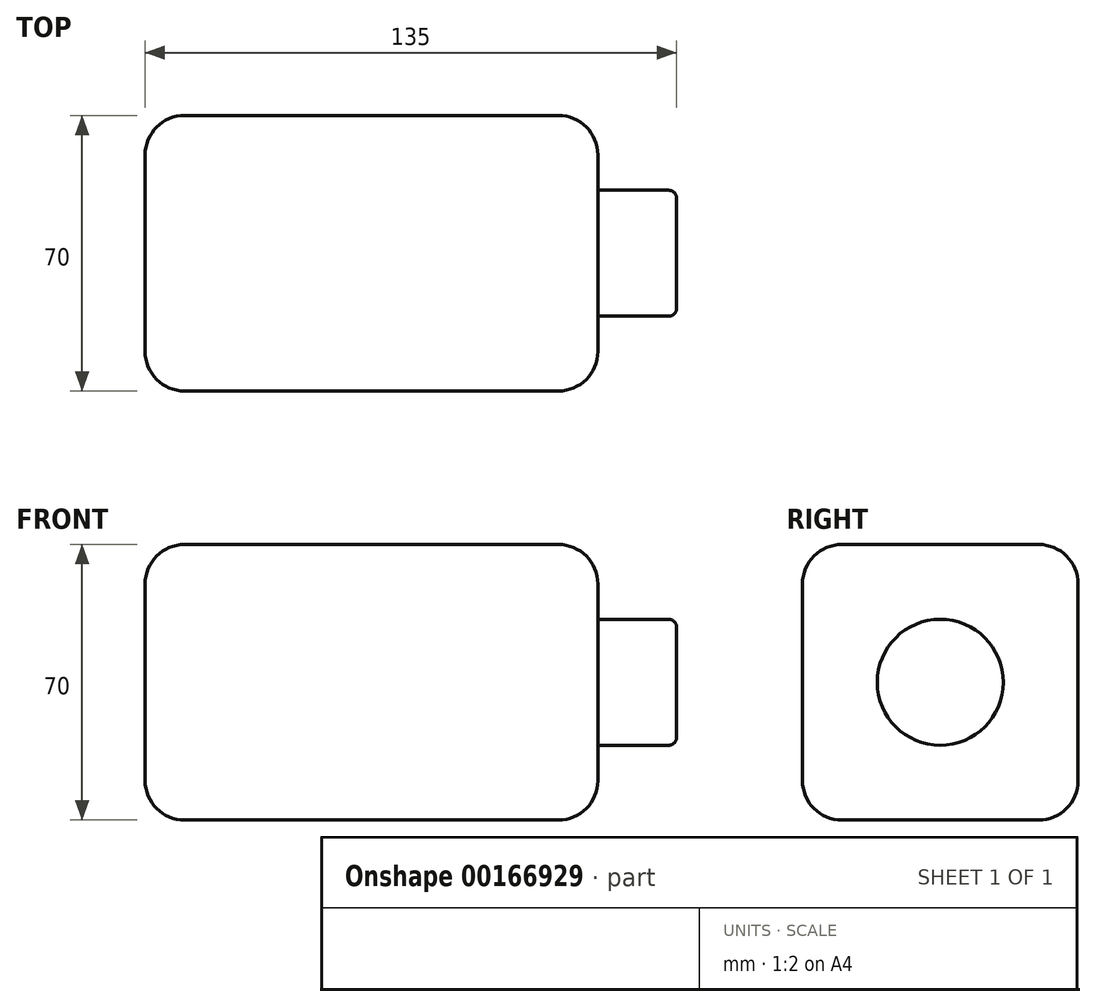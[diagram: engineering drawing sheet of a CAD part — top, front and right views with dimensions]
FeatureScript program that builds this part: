
annotation { "Feature Type Name" : "Feature", "Feature Type Description" : "" }
export const myFeature = defineFeature(function(context is Context, id is Id, definition is map)
    precondition{}
    {
        {
            var Q0;
            Q0=qCreatedBy(makeId("Right.planeOp"),FACE);
            var sketch = newSketch(context, id + "F0", { "sketchPlane" : qUnion([Q0])});
            skLineSegment(sketch, "E0.bottom", {"start": v(35, 35) * mm, "end": v(-35, 35) * mm});
            skLineSegment(sketch, "E0.top", {"start": v(35, -35) * mm, "end": v(-35, -35) * mm});
            skLineSegment(sketch, "E0.left", {"start": v(35, 35) * mm, "end": v(35, -35) * mm});
            skLineSegment(sketch, "E0.right", {"start": v(-35, 35) * mm, "end": v(-35, -35) * mm});
            skPoint(sketch, "E0.middle", {"position": v(0, 0) * mm});
            skSolve(sketch);
        }
        {
            var Q0;
            Q0=qSketchRegion(id+"F0",true);
            extrude(context, id + "F1", {"entities" : qUnion([Q0]), "endBound" : BoundingType.SYMMETRIC, "depth" : 115 * mm});
        }
        {
            var Q0;
            Q0=makeQuery(id+"F1.opExtrude","CAP_EDGE",EDGE,{"disambiguationData":[OSD([sQuery(id+"F0.wireOp",EDGE,"E0.right")])],"isStart":false});
            var Q1;
            Q1=makeQuery(id+"F1.opExtrude","CAP_EDGE",EDGE,{"disambiguationData":[OSD([sQuery(id+"F0.wireOp",EDGE,"E0.bottom")])],"isStart":false});
            var Q2;
            Q2=makeQuery(id+"F1.opExtrude","SWEPT_EDGE",EDGE,{"disambiguationData":[OSD([sQuery(id+"F0.wireOp",EDGE,"E0.bottom"),sQuery(id+"F0.wireOp",EDGE,"E0.right")])]});
            var Q3;
            Q3=makeQuery(id+"F1.opExtrude","CAP_EDGE",EDGE,{"disambiguationData":[OSD([sQuery(id+"F0.wireOp",EDGE,"E0.left")])],"isStart":false});
            var Q4;
            Q4=makeQuery(id+"F1.opExtrude","SWEPT_EDGE",EDGE,{"disambiguationData":[OSD([sQuery(id+"F0.wireOp",EDGE,"E0.bottom"),sQuery(id+"F0.wireOp",EDGE,"E0.left")])]});
            var Q5;
            Q5=makeQuery(id+"F1.opExtrude","CAP_EDGE",EDGE,{"disambiguationData":[OSD([sQuery(id+"F0.wireOp",EDGE,"E0.left")])],"isStart":true});
            var Q6;
            Q6=makeQuery(id+"F1.opExtrude","CAP_EDGE",EDGE,{"disambiguationData":[OSD([sQuery(id+"F0.wireOp",EDGE,"E0.right")])],"isStart":true});
            var Q7;
            Q7=makeQuery(id+"F1.opExtrude","SWEPT_EDGE",EDGE,{"disambiguationData":[OSD([sQuery(id+"F0.wireOp",EDGE,"E0.top"),sQuery(id+"F0.wireOp",EDGE,"E0.right")])]});
            var Q8;
            Q8=makeQuery(id+"F1.opExtrude","CAP_EDGE",EDGE,{"disambiguationData":[OSD([sQuery(id+"F0.wireOp",EDGE,"E0.top")])],"isStart":false});
            var Q9;
            Q9=makeQuery(id+"F1.opExtrude","CAP_EDGE",EDGE,{"disambiguationData":[OSD([sQuery(id+"F0.wireOp",EDGE,"E0.top")])],"isStart":true});
            var Q10;
            Q10=makeQuery(id+"F1.opExtrude","CAP_EDGE",EDGE,{"disambiguationData":[OSD([sQuery(id+"F0.wireOp",EDGE,"E0.bottom")])],"isStart":true});
            var Q11;
            Q11=makeQuery(id+"F1.opExtrude","SWEPT_EDGE",EDGE,{"disambiguationData":[OSD([sQuery(id+"F0.wireOp",EDGE,"E0.top"),sQuery(id+"F0.wireOp",EDGE,"E0.left")])]});
            fillet(context, id + "F2", {"entities" : qUnion([Q0, Q1, Q2, Q3, Q4, Q5, Q6, Q7, Q8, Q9, Q10, Q11]), "radius" : 10 * mm, "tangentPropagation" : true, "allowEdgeOverflow" : false});
        }
        {
            var Q0;
            Q0=qCreatedBy(makeId("Right.planeOp"),FACE);
            var sketch = newSketch(context, id + "F3", { "sketchPlane" : qUnion([Q0])});
            skCircle(sketch, "E1", {"center": v(0, 0) * mm, "radius": 16 * mm});
            skSolve(sketch);
        }
        {
            var Q0;
            Q0=qSketchRegion(id+"F3",true);
            extrude(context, id + "F4", {"entities" : qUnion([Q0]), "depth" : 20 * mm});
        }
        {
            var Q0;
            Q0=makeQuery(id+"F4.opExtrude","SWEPT_BODY",BODY,{"disambiguationData":[OSD([sQuery(id+"F3.wireOp",EDGE,"E1")])]});
            var Q1;
            Q1=qCreatedBy(makeId("Right.planeOp"),FACE);
            transform(context, id + "F5", {"entities" : qUnion([Q0]), "transformType" : TransformType.TRANSLATION_DISTANCE, "transformDirection" : qUnion([Q1]), "distance" : 57.5 * mm, "makeCopy" : false});
        }
        {
            var Q0;
            Q0=makeQuery(id+"F4.opExtrude","CAP_EDGE",EDGE,{"disambiguationData":[OSD([sQuery(id+"F3.wireOp",EDGE,"E1")])],"isStart":false});
            fillet(context, id + "F6", {"entities" : qUnion([Q0]), "radius" : 2 * mm, "tangentPropagation" : true, "allowEdgeOverflow" : false});
        }
    });
